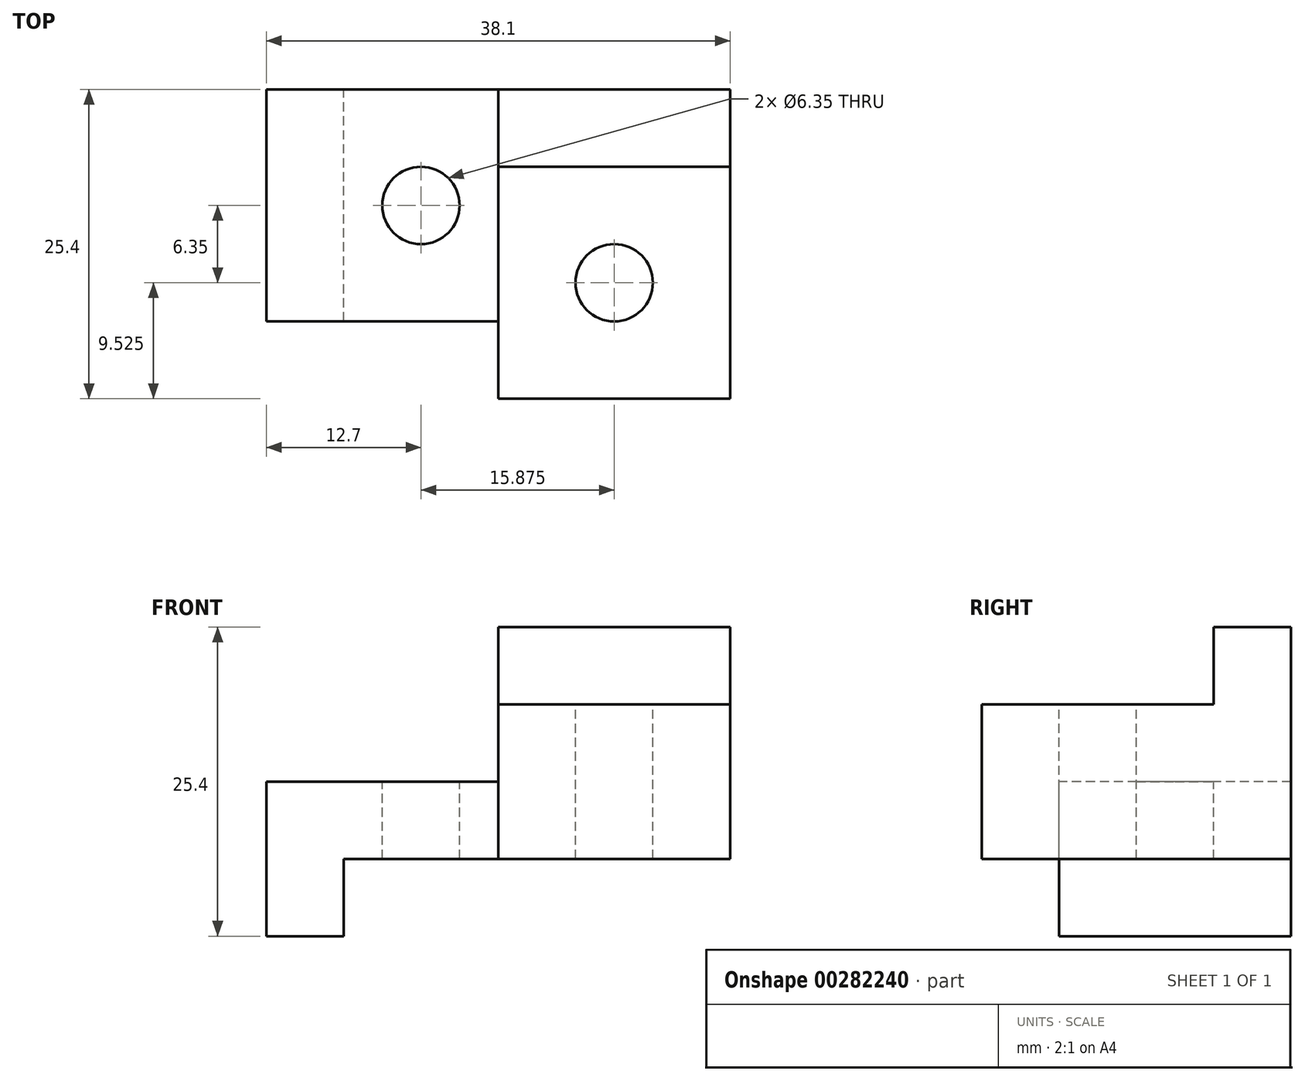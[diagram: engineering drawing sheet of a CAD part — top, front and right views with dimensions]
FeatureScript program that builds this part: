
annotation { "Feature Type Name" : "Feature", "Feature Type Description" : "" }
export const myFeature = defineFeature(function(context is Context, id is Id, definition is map)
    precondition{}
    {
        {
            var Q0;
            Q0=qCreatedBy(makeId("Right.planeOp"),FACE);
            var sketch = newSketch(context, id + "F0", { "sketchPlane" : qUnion([Q0])});
            skLineSegment(sketch, "E0.bottom", {"start": v(0, 0) * mm, "end": v(25.4, 0) * mm});
            skLineSegment(sketch, "E0.top", {"start": v(0, 19.05) * mm, "end": v(25.4, 19.05) * mm});
            skLineSegment(sketch, "E0.left", {"start": v(0, 0) * mm, "end": v(0, 19.05) * mm});
            skLineSegment(sketch, "E0.right", {"start": v(25.4, 0) * mm, "end": v(25.4, 19.05) * mm});
            skSolve(sketch);
        }
        {
            var Q0;
            Q0 = qSketchRegion(id + "F0", true);
            extrude(context, id + "F1", {"entities" : qUnion([Q0]), "depth" : 19.05 * mm});
        }
        {
            var Q0;
            Q0=makeQuery(id+"F1.opExtrude","CAP_FACE",FACE,{"disambiguationData":[OSD([sQuery(id+"F0.wireOp",EDGE,"E0.bottom"),sQuery(id+"F0.wireOp",EDGE,"E0.top"),sQuery(id+"F0.wireOp",EDGE,"E0.left"),sQuery(id+"F0.wireOp",EDGE,"E0.right")])],"isStart":false});
            var sketch = newSketch(context, id + "F2", { "sketchPlane" : qUnion([Q0])});
            skLineSegment(sketch, "E1.bottom", {"start": v(0, 19.05) * mm, "end": v(19.05, 19.05) * mm});
            skLineSegment(sketch, "E1.top", {"start": v(0, 12.7) * mm, "end": v(19.05, 12.7) * mm});
            skLineSegment(sketch, "E1.left", {"start": v(0, 19.05) * mm, "end": v(0, 12.7) * mm});
            skLineSegment(sketch, "E1.right", {"start": v(19.05, 19.05) * mm, "end": v(19.05, 12.7) * mm});
            skSolve(sketch);
        }
        {
            var Q0;
            Q0=makeQuery(id+"F2.imprint","IMPRINT",FACE,{"disambiguationData":[TD([[makeQuery(id+"F2.imprint","IMPRINT",EDGE,{"derivedFrom":sQuery(id+"F2.wireOp",EDGE,"E1.bottom")}),-1.0]])]});
            extrude(context, id + "F3", {"entities" : qUnion([Q0]), "operationType" : NewBodyOperationType.REMOVE, "oppositeDirection" : true, "depth" : 19.05 * mm});
        }
        {
            var Q0;
            Q0=makeQuery(id+"F1.opExtrude","CAP_FACE",FACE,{"disambiguationData":[OSD([sQuery(id+"F0.wireOp",EDGE,"E0.bottom"),sQuery(id+"F0.wireOp",EDGE,"E0.top"),sQuery(id+"F0.wireOp",EDGE,"E0.left"),sQuery(id+"F0.wireOp",EDGE,"E0.right")])],"isStart":true});
            var sketch = newSketch(context, id + "F4", { "sketchPlane" : qUnion([Q0])});
            skLineSegment(sketch, "E2.bottom", {"start": v(-25.4, 0) * mm, "end": v(-6.35, 0) * mm});
            skLineSegment(sketch, "E2.top", {"start": v(-25.4, 6.35) * mm, "end": v(-6.35, 6.35) * mm});
            skLineSegment(sketch, "E2.left", {"start": v(-25.4, 0) * mm, "end": v(-25.4, 6.35) * mm});
            skLineSegment(sketch, "E2.right", {"start": v(-6.35, 0) * mm, "end": v(-6.35, 6.35) * mm});
            skSolve(sketch);
        }
        {
            var Q0;
            Q0 = qSketchRegion(id + "F4", true);
            extrude(context, id + "F5", {"entities" : qUnion([Q0]), "operationType" : NewBodyOperationType.ADD, "depth" : 19.05 * mm});
        }
        {
            var Q0;
            Q0=makeQuery(id+"F5.boolean.opBoolean","MERGE",FACE,{"derivedFrom":[makeQuery(id+"F1.opExtrude","SWEPT_FACE",FACE,{"disambiguationData":[OSD([sQuery(id+"F0.wireOp",EDGE,"E0.bottom")])]}),makeQuery(id+"F5.opExtrude","SWEPT_FACE",FACE,{"disambiguationData":[OSD([sQuery(id+"F4.wireOp",EDGE,"E2.bottom")])]})]});
            var sketch = newSketch(context, id + "F6", { "sketchPlane" : qUnion([Q0])});
            skLineSegment(sketch, "E3.bottom", {"start": v(-19.05, -6.35) * mm, "end": v(-12.7, -6.35) * mm});
            skLineSegment(sketch, "E3.top", {"start": v(-19.05, -25.4) * mm, "end": v(-12.7, -25.4) * mm});
            skLineSegment(sketch, "E3.left", {"start": v(-19.05, -6.35) * mm, "end": v(-19.05, -25.4) * mm});
            skLineSegment(sketch, "E3.right", {"start": v(-12.7, -6.35) * mm, "end": v(-12.7, -25.4) * mm});
            skSolve(sketch);
        }
        {
            var Q0;
            Q0=makeQuery(id+"F6.imprint","IMPRINT",FACE,{"disambiguationData":[TD([[makeQuery(id+"F6.imprint","IMPRINT",EDGE,{"derivedFrom":sQuery(id+"F6.wireOp",EDGE,"E3.bottom")}),-1.0]])]});
            extrude(context, id + "F7", {"entities" : qUnion([Q0]), "operationType" : NewBodyOperationType.ADD, "depth" : 6.35 * mm});
        }
        {
            var Q0;
            Q0=makeQuery(id+"F3.boolean.opBoolean","COPY",FACE,{"derivedFrom":makeQuery(id+"F3.opExtrude","SWEPT_FACE",FACE,{"disambiguationData":[OSD([sQuery(id+"F2.wireOp",EDGE,"E1.top")])]})});
            var sketch = newSketch(context, id + "F8", { "sketchPlane" : qUnion([Q0])});
            skCircle(sketch, "E4", {"center": v(9.52, 9.53) * mm, "radius": 3.18 * mm});
            skPoint(sketch, "E4.centerSnap0", {"position": v(19.05, 9.53) * mm});
            skPoint(sketch, "E4.centerSnap1", {"position": v(9.52, 0) * mm});
            skSolve(sketch);
        }
        {
            var Q0;
            Q0=makeQuery(id+"F8.imprint","IMPRINT",FACE,{"disambiguationData":[TD([[makeQuery(id+"F8.imprint","IMPRINT",EDGE,{"derivedFrom":sQuery(id+"F8.wireOp",EDGE,"E4")}),1.0]])]});
            extrude(context, id + "F9", {"entities" : qUnion([Q0]), "operationType" : NewBodyOperationType.REMOVE, "oppositeDirection" : true, "depth" : 25.4 * mm});
        }
        {
            var Q0;
            Q0=makeQuery(id+"F5.opExtrude","SWEPT_FACE",FACE,{"disambiguationData":[OSD([sQuery(id+"F4.wireOp",EDGE,"E2.top")])]});
            var sketch = newSketch(context, id + "F10", { "sketchPlane" : qUnion([Q0])});
            skCircle(sketch, "E5", {"center": v(-6.35, 15.88) * mm, "radius": 3.18 * mm});
            skPoint(sketch, "E5.centerSnap0", {"position": v(0, 15.88) * mm});
            skSolve(sketch);
        }
        {
            var Q0;
            Q0=makeQuery(id+"F10.imprint","IMPRINT",FACE,{"disambiguationData":[TD([[makeQuery(id+"F10.imprint","IMPRINT",EDGE,{"derivedFrom":sQuery(id+"F10.wireOp",EDGE,"E5")}),1.0]])]});
            extrude(context, id + "F11", {"entities" : qUnion([Q0]), "operationType" : NewBodyOperationType.REMOVE, "oppositeDirection" : true, "depth" : 6.35 * mm});
        }
    });
